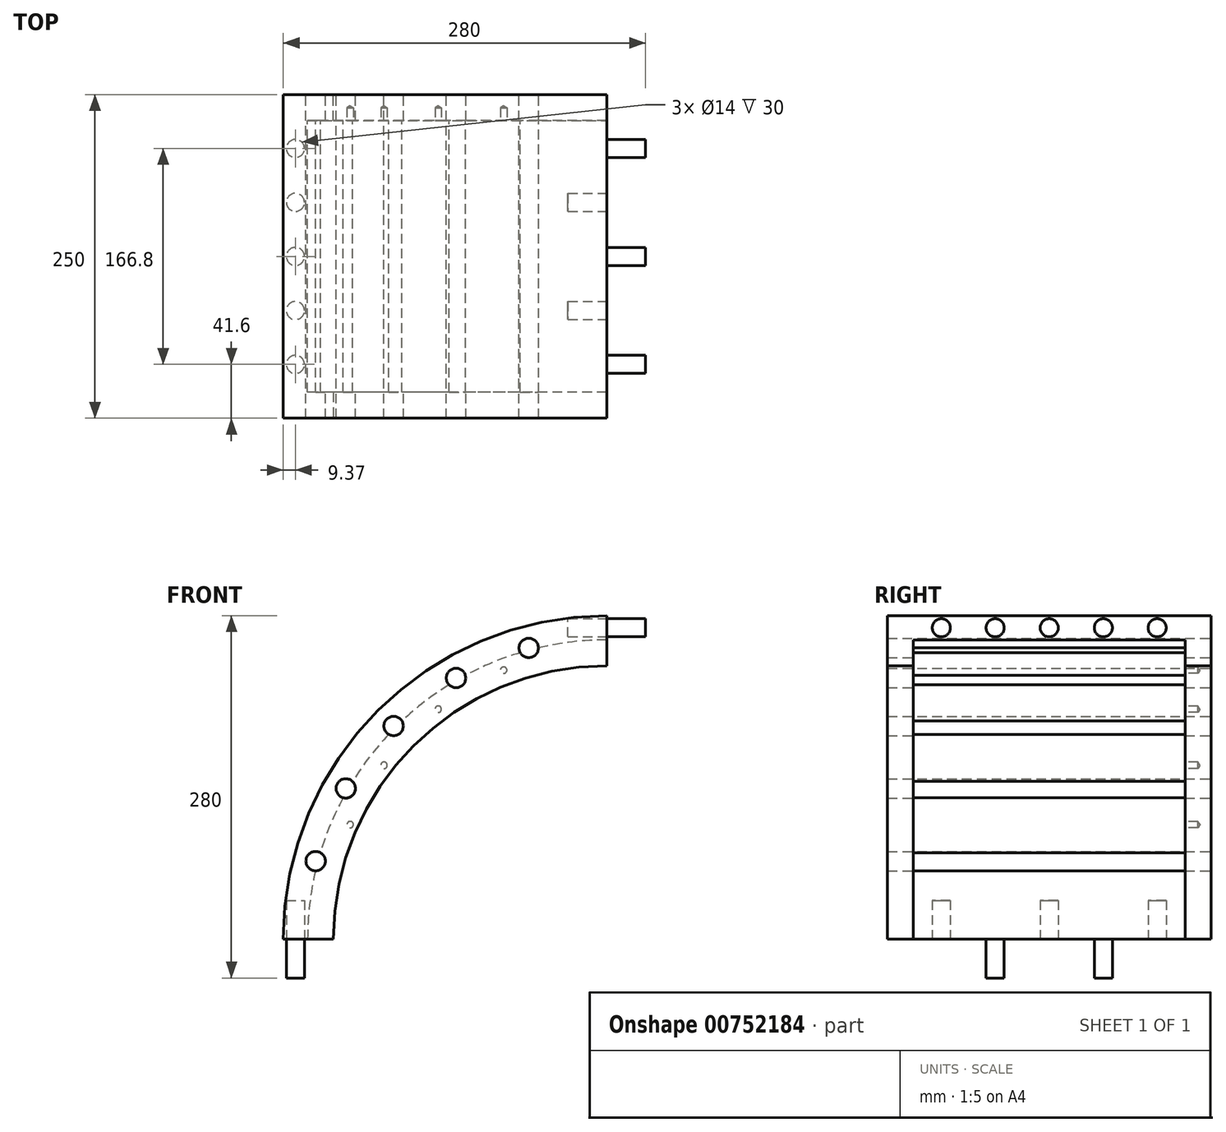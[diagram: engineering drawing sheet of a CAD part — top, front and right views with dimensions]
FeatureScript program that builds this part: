
annotation { "Feature Type Name" : "Feature", "Feature Type Description" : "" }
export const myFeature = defineFeature(function(context is Context, id is Id, definition is map)
    precondition{}
    {
        {
            var Q0;
            Q0=qCreatedBy(makeId("Front.planeOp"),FACE);
            var sketch = newSketch(context, id + "F0", { "sketchPlane" : qUnion([Q0])});
            skLineSegment(sketch, "E0.bottom", {"start": v(-250, 250) * mm, "end": v(250, 250) * mm});
            skLineSegment(sketch, "E0.top", {"start": v(-250, -250) * mm, "end": v(250, -250) * mm});
            skLineSegment(sketch, "E0.left", {"start": v(-250, 250) * mm, "end": v(-250, -250) * mm});
            skLineSegment(sketch, "E0.right", {"start": v(250, 250) * mm, "end": v(250, -250) * mm});
            skPoint(sketch, "E0.middle", {"position": v(0, 0) * mm});
            skCircle(sketch, "E1", {"center": v(0, 0) * mm, "radius": 250 * mm});
            skLineSegment(sketch, "E2", {"start": v(0, 0) * mm, "end": v(0, 250) * mm, "construction": true});
            skLineSegment(sketch, "E3", {"start": v(0, -250) * mm, "end": v(0, 0) * mm, "construction": true});
            skLineSegment(sketch, "E4", {"start": v(-250, 0) * mm, "end": v(250, 0) * mm, "construction": true});
            skCircle(sketch, "E5", {"center": v(0, 0) * mm, "radius": 231.25 * mm});
            skLineSegment(sketch, "E6", {"start": v(0, 250) * mm, "end": v(0, 0) * mm});
            skLineSegment(sketch, "E7", {"start": v(-250, 0) * mm, "end": v(0, 0) * mm});
            skSolve(sketch);
        }
        {
            var Q0;
            {var subQ0=sQuery(id+"F0.wireOp",EDGE,"E6");var subQ5=sQuery(id+"F0.wireOp",EDGE,"E5");var subQ6=makeQuery(id+"F0.imprint","INTERSECT",VERTEX,{"derivedFrom":[subQ5,subQ0]});Q0=makeQuery(id+"F0.imprint","IMPRINT",FACE,{"disambiguationData":[TD([[makeQuery(id+"F0.imprint","IMPRINT",EDGE,{"disambiguationData":[TD([[subQ6,-1.0]])],"derivedFrom":subQ5}),-1.0]])]});}
            extrude(context, id + "F1", {"entities" : qUnion([Q0]), "depth" : 250 * mm, "offsetDistance" : 25 * mm});
        }
        {
            var Q0;
            Q0=makeQuery(id+"F1.opExtrude","SWEPT_FACE",FACE,{"disambiguationData":[OSD([sQuery(id+"F0.wireOp",EDGE,"E6")])]});
            var sketch = newSketch(context, id + "F2", { "sketchPlane" : qUnion([Q0])});
            skLineSegment(sketch, "E8", {"start": v(-250, 240.63) * mm, "end": v(0, 240.63) * mm, "construction": true});
            skLineSegment(sketch, "E9", {"start": v(-125, 250) * mm, "end": v(-125, 231.25) * mm, "construction": true});
            skLineSegment(sketch, "E10", {"start": v(-208.4, 250) * mm, "end": v(-208.4, 231.25) * mm, "construction": true});
            skLineSegment(sketch, "E11", {"start": v(-166.8, 250) * mm, "end": v(-166.8, 231.25) * mm, "construction": true});
            skLineSegment(sketch, "E12", {"start": v(-83.2, 250) * mm, "end": v(-83.2, 231.25) * mm, "construction": true});
            skLineSegment(sketch, "E13", {"start": v(-41.6, 250) * mm, "end": v(-41.6, 231.25) * mm, "construction": true});
            skPoint(sketch, "E14", {"position": v(-208.4, 240.62) * mm});
            skPoint(sketch, "E15", {"position": v(-166.8, 240.62) * mm});
            skPoint(sketch, "E16", {"position": v(-125, 240.63) * mm});
            skPoint(sketch, "E17", {"position": v(-83.2, 240.63) * mm});
            skPoint(sketch, "E18", {"position": v(-41.6, 240.62) * mm});
            skCircle(sketch, "E19", {"center": v(-208.4, 240.62) * mm, "radius": 7 * mm});
            skCircle(sketch, "E20", {"center": v(-166.8, 240.62) * mm, "radius": 7 * mm});
            skCircle(sketch, "E21", {"center": v(-125, 240.63) * mm, "radius": 7 * mm});
            skCircle(sketch, "E22", {"center": v(-83.2, 240.63) * mm, "radius": 7 * mm});
            skCircle(sketch, "E23", {"center": v(-41.6, 240.62) * mm, "radius": 7 * mm});
            skSolve(sketch);
        }
        {
            var Q0;
            Q0=makeQuery(id+"F2.imprint","IMPRINT",FACE,{"disambiguationData":[TD([[makeQuery(id+"F2.imprint","IMPRINT",EDGE,{"derivedFrom":sQuery(id+"F2.wireOp",EDGE,"E19")}),1.0]])]});
            var Q1;
            Q1=makeQuery(id+"F2.imprint","IMPRINT",FACE,{"disambiguationData":[TD([[makeQuery(id+"F2.imprint","IMPRINT",EDGE,{"derivedFrom":sQuery(id+"F2.wireOp",EDGE,"E21")}),1.0]])]});
            var Q2;
            Q2=makeQuery(id+"F2.imprint","IMPRINT",FACE,{"disambiguationData":[TD([[makeQuery(id+"F2.imprint","IMPRINT",EDGE,{"derivedFrom":sQuery(id+"F2.wireOp",EDGE,"E23")}),1.0]])]});
            extrude(context, id + "F3", {"entities" : qUnion([Q0, Q1, Q2]), "operationType" : NewBodyOperationType.ADD, "depth" : 30 * mm, "offsetDistance" : 25 * mm});
        }
        {
            var Q0;
            Q0=makeQuery(id+"F2.imprint","IMPRINT",FACE,{"disambiguationData":[TD([[makeQuery(id+"F2.imprint","IMPRINT",EDGE,{"derivedFrom":sQuery(id+"F2.wireOp",EDGE,"E20")}),1.0]])]});
            var Q1;
            Q1=makeQuery(id+"F2.imprint","IMPRINT",FACE,{"disambiguationData":[TD([[makeQuery(id+"F2.imprint","IMPRINT",EDGE,{"derivedFrom":sQuery(id+"F2.wireOp",EDGE,"E22")}),1.0]])]});
            extrude(context, id + "F4", {"entities" : qUnion([Q0, Q1]), "operationType" : NewBodyOperationType.REMOVE, "oppositeDirection" : true, "depth" : 30 * mm, "offsetDistance" : 25 * mm});
        }
        {
            var Q0;
            Q0=makeQuery(id+"F1.opExtrude","CAP_FACE",FACE,{"disambiguationData":[OSD([sQuery(id+"F0.wireOp",EDGE,"E1"),sQuery(id+"F0.wireOp",EDGE,"E5"),sQuery(id+"F0.wireOp",EDGE,"E6"),sQuery(id+"F0.wireOp",EDGE,"E7")])],"isStart":false});
            var sketch = newSketch(context, id + "F5", { "sketchPlane" : qUnion([Q0])});
            skCircle(sketch, "E24", {"center": v(0, 0) * mm, "radius": 211.25 * mm});
            skPoint(sketch, "E25", {"position": v(-211.25, 0) * mm});
            skPoint(sketch, "E26", {"position": v(0, 211.25) * mm});
            skLineSegment(sketch, "E27", {"start": v(0, 231.25) * mm, "end": v(0, 211.25) * mm});
            skLineSegment(sketch, "E28", {"start": v(-211.25, 0) * mm, "end": v(-231.25, 0) * mm});
            skArc(sketch, "E29", {"start": v(-231.25, 0) * mm, "mid": v(-163.52, 163.52) * mm, "end": v(0, 231.25) * mm});
            skSolve(sketch);
        }
        {
            var Q0;
            {var subQ0=sQuery(id+"F5.wireOp",EDGE,"E27");Q0=makeQuery(id+"F5.imprint","IMPRINT",FACE,{"disambiguationData":[TD([[makeQuery(id+"F5.imprint","IMPRINT",EDGE,{"derivedFrom":subQ0}),-1.0]])]});}
            extrude(context, id + "F6", {"entities" : qUnion([Q0]), "operationType" : NewBodyOperationType.ADD, "oppositeDirection" : true, "depth" : 20 * mm, "offsetDistance" : 25 * mm});
        }
        {
            var Q0;
            Q0=makeQuery(id+"F1.opExtrude","CAP_FACE",FACE,{"disambiguationData":[OSD([sQuery(id+"F0.wireOp",EDGE,"E1"),sQuery(id+"F0.wireOp",EDGE,"E5"),sQuery(id+"F0.wireOp",EDGE,"E6"),sQuery(id+"F0.wireOp",EDGE,"E7")])],"isStart":true});
            var sketch = newSketch(context, id + "F7", { "sketchPlane" : qUnion([Q0])});
            skCircle(sketch, "E30", {"center": v(0, 0) * mm, "radius": 211.25 * mm});
            skLineSegment(sketch, "E31", {"start": v(0, 231.25) * mm, "end": v(0, 211.25) * mm});
            skLineSegment(sketch, "E32", {"start": v(231.25, 0) * mm, "end": v(211.25, 0) * mm});
            skSolve(sketch);
        }
        {
            var Q0;
            {var subQ0=sQuery(id+"F7.wireOp",EDGE,"E31");Q0=makeQuery(id+"F7.imprint","IMPRINT",FACE,{"disambiguationData":[TD([[makeQuery(id+"F7.imprint","IMPRINT",EDGE,{"derivedFrom":subQ0}),1.0]])]});}
            extrude(context, id + "F8", {"entities" : qUnion([Q0]), "operationType" : NewBodyOperationType.ADD, "oppositeDirection" : true, "depth" : 20 * mm, "offsetDistance" : 25 * mm});
        }
        {
            var Q0;
            Q0=makeQuery(id+"F8.boolean.opBoolean","MERGE",FACE,{"derivedFrom":[makeQuery(id+"F6.boolean.opBoolean","MERGE",FACE,{"derivedFrom":[makeQuery(id+"F1.opExtrude","SWEPT_FACE",FACE,{"disambiguationData":[OSD([sQuery(id+"F0.wireOp",EDGE,"E7")])]}),makeQuery(id+"F6.opExtrude","SWEPT_FACE",FACE,{"disambiguationData":[OSD([sQuery(id+"F5.wireOp",EDGE,"E28")])]})]}),makeQuery(id+"F8.opExtrude","SWEPT_FACE",FACE,{"disambiguationData":[OSD([sQuery(id+"F7.wireOp",EDGE,"E32")])]})]});
            var sketch = newSketch(context, id + "F9", { "sketchPlane" : qUnion([Q0])});
            skLineSegment(sketch, "E33", {"start": v(-231.25, 125) * mm, "end": v(-250, 125) * mm, "construction": true});
            skLineSegment(sketch, "E34", {"start": v(-250, 41.6) * mm, "end": v(-231.25, 41.6) * mm});
            skLineSegment(sketch, "E35", {"start": v(-250, 83.2) * mm, "end": v(-231.25, 83.2) * mm});
            skLineSegment(sketch, "E36", {"start": v(-250, 208.4) * mm, "end": v(-231.25, 208.4) * mm});
            skLineSegment(sketch, "E37", {"start": v(-250, 166.8) * mm, "end": v(-231.25, 166.8) * mm});
            skLineSegment(sketch, "E38", {"start": v(-250, 125) * mm, "end": v(-231.25, 125) * mm});
            skLineSegment(sketch, "E39", {"start": v(-240.63, 41.6) * mm, "end": v(-240.63, 250) * mm});
            skLineSegment(sketch, "E40", {"start": v(-240.63, 250) * mm, "end": v(-240.63, 0) * mm});
            skCircle(sketch, "E41", {"center": v(-240.63, 208.4) * mm, "radius": 7 * mm});
            skCircle(sketch, "E42", {"center": v(-240.63, 166.8) * mm, "radius": 7 * mm});
            skCircle(sketch, "E43", {"center": v(-240.63, 125) * mm, "radius": 7 * mm});
            skCircle(sketch, "E44", {"center": v(-240.63, 83.2) * mm, "radius": 7 * mm});
            skCircle(sketch, "E45", {"center": v(-240.63, 41.6) * mm, "radius": 7 * mm});
            skSolve(sketch);
        }
        {
            var Q0;
            {var subQ0=sQuery(id+"F9.wireOp",EDGE,"E40");var subQ1=sQuery(id+"F9.wireOp",EDGE,"E37");var subQ2=makeQuery(id+"F9.imprint","INTERSECT",VERTEX,{"derivedFrom":[subQ1,subQ0]});Q0=makeQuery(id+"F9.imprint","IMPRINT",FACE,{"disambiguationData":[TD([[makeQuery(id+"F9.imprint","IMPRINT",EDGE,{"disambiguationData":[TD([[subQ2,-1.0]])],"derivedFrom":subQ1}),1.0]])]});}
            var Q1;
            {var subQ0=sQuery(id+"F9.wireOp",EDGE,"E40");var subQ1=sQuery(id+"F9.wireOp",EDGE,"E37");var subQ2=makeQuery(id+"F9.imprint","INTERSECT",VERTEX,{"derivedFrom":[subQ1,subQ0]});Q1=makeQuery(id+"F9.imprint","IMPRINT",FACE,{"disambiguationData":[TD([[makeQuery(id+"F9.imprint","IMPRINT",EDGE,{"disambiguationData":[TD([[subQ2,-1.0]])],"derivedFrom":subQ1}),-1.0]])]});}
            var Q2;
            {var subQ0=sQuery(id+"F9.wireOp",EDGE,"E42");var subQ1=sQuery(id+"F9.wireOp",EDGE,"E37");var subQ2=makeQuery(id+"F9.imprint","INTERSECT",VERTEX,{"disambiguationData":[OD(0.0)],"derivedFrom":[subQ1,subQ0]});Q2=makeQuery(id+"F9.imprint","IMPRINT",FACE,{"disambiguationData":[TD([[makeQuery(id+"F9.imprint","IMPRINT",EDGE,{"disambiguationData":[TD([[subQ2,-1.0]])],"derivedFrom":subQ1}),-1.0]])]});}
            var Q3;
            {var subQ0=sQuery(id+"F9.wireOp",EDGE,"E42");var subQ1=sQuery(id+"F9.wireOp",EDGE,"E37");var subQ2=makeQuery(id+"F9.imprint","INTERSECT",VERTEX,{"disambiguationData":[OD(0.0)],"derivedFrom":[subQ1,subQ0]});Q3=makeQuery(id+"F9.imprint","IMPRINT",FACE,{"disambiguationData":[TD([[makeQuery(id+"F9.imprint","IMPRINT",EDGE,{"disambiguationData":[TD([[subQ2,-1.0]])],"derivedFrom":subQ1}),1.0]])]});}
            var Q4;
            {var subQ0=sQuery(id+"F9.wireOp",EDGE,"E40");var subQ1=sQuery(id+"F9.wireOp",EDGE,"E35");var subQ2=makeQuery(id+"F9.imprint","INTERSECT",VERTEX,{"derivedFrom":[subQ1,subQ0]});Q4=makeQuery(id+"F9.imprint","IMPRINT",FACE,{"disambiguationData":[TD([[makeQuery(id+"F9.imprint","IMPRINT",EDGE,{"disambiguationData":[TD([[subQ2,-1.0]])],"derivedFrom":subQ1}),1.0]])]});}
            var Q5;
            {var subQ0=sQuery(id+"F9.wireOp",EDGE,"E40");var subQ1=sQuery(id+"F9.wireOp",EDGE,"E35");var subQ2=makeQuery(id+"F9.imprint","INTERSECT",VERTEX,{"derivedFrom":[subQ1,subQ0]});Q5=makeQuery(id+"F9.imprint","IMPRINT",FACE,{"disambiguationData":[TD([[makeQuery(id+"F9.imprint","IMPRINT",EDGE,{"disambiguationData":[TD([[subQ2,-1.0]])],"derivedFrom":subQ1}),-1.0]])]});}
            var Q6;
            {var subQ0=sQuery(id+"F9.wireOp",EDGE,"E44");var subQ1=sQuery(id+"F9.wireOp",EDGE,"E35");var subQ2=makeQuery(id+"F9.imprint","INTERSECT",VERTEX,{"disambiguationData":[OD(0.0)],"derivedFrom":[subQ1,subQ0]});Q6=makeQuery(id+"F9.imprint","IMPRINT",FACE,{"disambiguationData":[TD([[makeQuery(id+"F9.imprint","IMPRINT",EDGE,{"disambiguationData":[TD([[subQ2,-1.0]])],"derivedFrom":subQ1}),1.0]])]});}
            var Q7;
            {var subQ0=sQuery(id+"F9.wireOp",EDGE,"E44");var subQ1=sQuery(id+"F9.wireOp",EDGE,"E35");var subQ2=makeQuery(id+"F9.imprint","INTERSECT",VERTEX,{"disambiguationData":[OD(0.0)],"derivedFrom":[subQ1,subQ0]});Q7=makeQuery(id+"F9.imprint","IMPRINT",FACE,{"disambiguationData":[TD([[makeQuery(id+"F9.imprint","IMPRINT",EDGE,{"disambiguationData":[TD([[subQ2,-1.0]])],"derivedFrom":subQ1}),-1.0]])]});}
            extrude(context, id + "F10", {"entities" : qUnion([Q0, Q1, Q2, Q3, Q4, Q5, Q6, Q7]), "operationType" : NewBodyOperationType.ADD, "depth" : 30 * mm, "offsetDistance" : 25 * mm});
        }
        {
            var Q0;
            {var subQ0=sQuery(id+"F9.wireOp",EDGE,"E41");var subQ1=sQuery(id+"F9.wireOp",EDGE,"E36");var subQ2=makeQuery(id+"F9.imprint","INTERSECT",VERTEX,{"disambiguationData":[OD(0.0)],"derivedFrom":[subQ1,subQ0]});Q0=makeQuery(id+"F9.imprint","IMPRINT",FACE,{"disambiguationData":[TD([[makeQuery(id+"F9.imprint","IMPRINT",EDGE,{"disambiguationData":[TD([[subQ2,-1.0]])],"derivedFrom":subQ1}),1.0]])]});}
            var Q1;
            {var subQ0=sQuery(id+"F9.wireOp",EDGE,"E40");var subQ1=sQuery(id+"F9.wireOp",EDGE,"E36");var subQ2=makeQuery(id+"F9.imprint","INTERSECT",VERTEX,{"derivedFrom":[subQ1,subQ0]});Q1=makeQuery(id+"F9.imprint","IMPRINT",FACE,{"disambiguationData":[TD([[makeQuery(id+"F9.imprint","IMPRINT",EDGE,{"disambiguationData":[TD([[subQ2,-1.0]])],"derivedFrom":subQ1}),1.0]])]});}
            var Q2;
            {var subQ0=sQuery(id+"F9.wireOp",EDGE,"E40");var subQ1=sQuery(id+"F9.wireOp",EDGE,"E36");var subQ2=makeQuery(id+"F9.imprint","INTERSECT",VERTEX,{"derivedFrom":[subQ1,subQ0]});Q2=makeQuery(id+"F9.imprint","IMPRINT",FACE,{"disambiguationData":[TD([[makeQuery(id+"F9.imprint","IMPRINT",EDGE,{"disambiguationData":[TD([[subQ2,-1.0]])],"derivedFrom":subQ1}),-1.0]])]});}
            var Q3;
            {var subQ0=sQuery(id+"F9.wireOp",EDGE,"E40");var subQ1=sQuery(id+"F9.wireOp",EDGE,"E38");var subQ2=makeQuery(id+"F9.imprint","INTERSECT",VERTEX,{"derivedFrom":[subQ1,subQ0]});Q3=makeQuery(id+"F9.imprint","IMPRINT",FACE,{"disambiguationData":[TD([[makeQuery(id+"F9.imprint","IMPRINT",EDGE,{"disambiguationData":[TD([[subQ2,-1.0]])],"derivedFrom":subQ1}),1.0]])]});}
            var Q4;
            {var subQ0=sQuery(id+"F9.wireOp",EDGE,"E43");var subQ1=sQuery(id+"F9.wireOp",EDGE,"E38");var subQ2=makeQuery(id+"F9.imprint","INTERSECT",VERTEX,{"disambiguationData":[OD(0.0)],"derivedFrom":[subQ1,subQ0]});Q4=makeQuery(id+"F9.imprint","IMPRINT",FACE,{"disambiguationData":[TD([[makeQuery(id+"F9.imprint","IMPRINT",EDGE,{"disambiguationData":[TD([[subQ2,-1.0]])],"derivedFrom":subQ1}),-1.0]])]});}
            var Q5;
            {var subQ0=sQuery(id+"F9.wireOp",EDGE,"E40");var subQ1=sQuery(id+"F9.wireOp",EDGE,"E38");var subQ2=makeQuery(id+"F9.imprint","INTERSECT",VERTEX,{"derivedFrom":[subQ1,subQ0]});Q5=makeQuery(id+"F9.imprint","IMPRINT",FACE,{"disambiguationData":[TD([[makeQuery(id+"F9.imprint","IMPRINT",EDGE,{"disambiguationData":[TD([[subQ2,-1.0]])],"derivedFrom":subQ1}),-1.0]])]});}
            var Q6;
            {var subQ0=sQuery(id+"F9.wireOp",EDGE,"E43");var subQ1=sQuery(id+"F9.wireOp",EDGE,"E38");var subQ2=makeQuery(id+"F9.imprint","INTERSECT",VERTEX,{"disambiguationData":[OD(0.0)],"derivedFrom":[subQ1,subQ0]});Q6=makeQuery(id+"F9.imprint","IMPRINT",FACE,{"disambiguationData":[TD([[makeQuery(id+"F9.imprint","IMPRINT",EDGE,{"disambiguationData":[TD([[subQ2,-1.0]])],"derivedFrom":subQ1}),1.0]])]});}
            var Q7;
            {var subQ0=sQuery(id+"F9.wireOp",EDGE,"E40");var subQ1=sQuery(id+"F9.wireOp",EDGE,"E34");var subQ2=makeQuery(id+"F9.imprint","INTERSECT",VERTEX,{"derivedFrom":[subQ1,subQ0]});Q7=makeQuery(id+"F9.imprint","IMPRINT",FACE,{"disambiguationData":[TD([[makeQuery(id+"F9.imprint","IMPRINT",EDGE,{"disambiguationData":[TD([[subQ2,-1.0]])],"derivedFrom":subQ1}),1.0]])]});}
            var Q8;
            {var subQ0=sQuery(id+"F9.wireOp",EDGE,"E40");var subQ1=sQuery(id+"F9.wireOp",EDGE,"E34");var subQ2=makeQuery(id+"F9.imprint","INTERSECT",VERTEX,{"derivedFrom":[subQ1,subQ0]});Q8=makeQuery(id+"F9.imprint","IMPRINT",FACE,{"disambiguationData":[TD([[makeQuery(id+"F9.imprint","IMPRINT",EDGE,{"disambiguationData":[TD([[subQ2,-1.0]])],"derivedFrom":subQ1}),-1.0]])]});}
            var Q9;
            {var subQ0=sQuery(id+"F9.wireOp",EDGE,"E45");var subQ1=sQuery(id+"F9.wireOp",EDGE,"E34");var subQ2=makeQuery(id+"F9.imprint","INTERSECT",VERTEX,{"disambiguationData":[OD(0.0)],"derivedFrom":[subQ1,subQ0]});Q9=makeQuery(id+"F9.imprint","IMPRINT",FACE,{"disambiguationData":[TD([[makeQuery(id+"F9.imprint","IMPRINT",EDGE,{"disambiguationData":[TD([[subQ2,-1.0]])],"derivedFrom":subQ1}),1.0]])]});}
            var Q10;
            {var subQ0=sQuery(id+"F9.wireOp",EDGE,"E45");var subQ1=sQuery(id+"F9.wireOp",EDGE,"E34");var subQ2=makeQuery(id+"F9.imprint","INTERSECT",VERTEX,{"disambiguationData":[OD(0.0)],"derivedFrom":[subQ1,subQ0]});Q10=makeQuery(id+"F9.imprint","IMPRINT",FACE,{"disambiguationData":[TD([[makeQuery(id+"F9.imprint","IMPRINT",EDGE,{"disambiguationData":[TD([[subQ2,-1.0]])],"derivedFrom":subQ1}),-1.0]])]});}
            var Q11;
            {var subQ0=sQuery(id+"F9.wireOp",EDGE,"E41");var subQ1=sQuery(id+"F9.wireOp",EDGE,"E36");var subQ2=makeQuery(id+"F9.imprint","INTERSECT",VERTEX,{"disambiguationData":[OD(0.0)],"derivedFrom":[subQ1,subQ0]});Q11=makeQuery(id+"F9.imprint","IMPRINT",FACE,{"disambiguationData":[TD([[makeQuery(id+"F9.imprint","IMPRINT",EDGE,{"disambiguationData":[TD([[subQ2,-1.0]])],"derivedFrom":subQ1}),-1.0]])]});}
            extrude(context, id + "F11", {"entities" : qUnion([Q0, Q1, Q2, Q3, Q4, Q5, Q6, Q7, Q8, Q9, Q10, Q11]), "operationType" : NewBodyOperationType.REMOVE, "oppositeDirection" : true, "depth" : 30 * mm, "offsetDistance" : 25 * mm});
        }
        {
            var Q0;
            {var subQ0=sQuery(id+"F0.wireOp",EDGE,"E5");Q0=makeQuery(id+"F8.boolean.opBoolean","MERGE",FACE,{"derivedFrom":[makeQuery(id+"F1.opExtrude","CAP_FACE",FACE,{"disambiguationData":[OSD([sQuery(id+"F0.wireOp",EDGE,"E1"),subQ0,sQuery(id+"F0.wireOp",EDGE,"E6"),sQuery(id+"F0.wireOp",EDGE,"E7")])],"isStart":true}),makeQuery(id+"F8.opExtrude","CAP_FACE",FACE,{"disambiguationData":[OSD([subQ0,sQuery(id+"F7.wireOp",EDGE,"E30"),sQuery(id+"F7.wireOp",EDGE,"E31"),sQuery(id+"F7.wireOp",EDGE,"E32")])],"isStart":true})]});}
            var sketch = newSketch(context, id + "F12", { "sketchPlane" : qUnion([Q0])});
            skLineSegment(sketch, "E46", {"start": v(0, 0) * mm, "end": v(0, 232.97) * mm, "construction": true});
            skLineSegment(sketch, "E47", {"start": v(0, 0) * mm, "end": v(232.97, 0) * mm, "construction": true});
            skLineSegment(sketch, "E48", {"start": v(0, 0) * mm, "end": v(164.73, 164.73) * mm, "construction": true});
            skLineSegment(sketch, "E49", {"start": v(0, 0) * mm, "end": v(116.48, 201.76) * mm, "construction": true});
            skLineSegment(sketch, "E50", {"start": v(0, 0) * mm, "end": v(201.76, 116.48) * mm, "construction": true});
            skLineSegment(sketch, "E51", {"start": v(0, 0) * mm, "end": v(60.3, 225.03) * mm, "construction": true});
            skLineSegment(sketch, "E52", {"start": v(0, 0) * mm, "end": v(225.03, 60.3) * mm, "construction": true});
            skLineSegment(sketch, "E53", {"start": v(0, 232.97) * mm, "end": v(60.3, 225.03) * mm, "construction": true});
            skLineSegment(sketch, "E54", {"start": v(60.3, 225.03) * mm, "end": v(116.48, 201.76) * mm, "construction": true});
            skLineSegment(sketch, "E55", {"start": v(116.48, 201.76) * mm, "end": v(164.73, 164.73) * mm, "construction": true});
            skLineSegment(sketch, "E56", {"start": v(164.73, 164.73) * mm, "end": v(201.76, 116.48) * mm, "construction": true});
            skLineSegment(sketch, "E57", {"start": v(201.76, 116.48) * mm, "end": v(225.03, 60.3) * mm, "construction": true});
            skLineSegment(sketch, "E58", {"start": v(225.03, 60.3) * mm, "end": v(232.97, 0) * mm, "construction": true});
            skPoint(sketch, "E59", {"position": v(60.3, 225.03) * mm});
            skPoint(sketch, "E60", {"position": v(116.48, 201.76) * mm});
            skPoint(sketch, "E61", {"position": v(164.73, 164.73) * mm});
            skPoint(sketch, "E62", {"position": v(201.76, 116.48) * mm});
            skPoint(sketch, "E63", {"position": v(225.03, 60.3) * mm});
            skLineSegment(sketch, "E64", {"start": v(247.82, 32.98) * mm, "end": v(0, 0) * mm, "construction": true});
            skSolve(sketch);
        }
        {
            var Q0;
            Q0=sQuery(id+"F12.wireOp",VERTEX,"E59");
            var Q1;
            Q1=sQuery(id+"F12.wireOp",VERTEX,"E60");
            var Q2;
            Q2=sQuery(id+"F12.wireOp",VERTEX,"E61");
            var Q3;
            Q3=sQuery(id+"F12.wireOp",VERTEX,"E62");
            var Q4;
            Q4=sQuery(id+"F12.wireOp",VERTEX,"E63");
            var Q5;
            Q5=makeQuery(id+"F1.opExtrude","SWEPT_BODY",BODY,{"disambiguationData":[OSD([sQuery(id+"F0.wireOp",EDGE,"E1"),sQuery(id+"F0.wireOp",EDGE,"E5"),sQuery(id+"F0.wireOp",EDGE,"E6"),sQuery(id+"F0.wireOp",EDGE,"E7")])]});
            hole(context, id + "F13", {"style" : HoleStyle.SIMPLE, "endStyle" : HoleEndStyle.BLIND, "holeDiameter" : 15 * mm, "majorDiameter" : 5 * mm, "holeDepth" : 400 * mm, "isTappedThrough" : true, "tappedDepth" : 12 * mm, "tapClearance" : 3, "startFromSketch" : true, "locations" : qUnion([Q0, Q1, Q2, Q3, Q4]), "scope" : qUnion([Q5])});
        }
        {
            var Q0;
            Q0=makeQuery(id+"F8.opExtrude","CAP_FACE",FACE,{"disambiguationData":[OSD([sQuery(id+"F0.wireOp",EDGE,"E5"),sQuery(id+"F7.wireOp",EDGE,"E30"),sQuery(id+"F7.wireOp",EDGE,"E31"),sQuery(id+"F7.wireOp",EDGE,"E32")])],"isStart":false});
            var sketch = newSketch(context, id + "F14", { "sketchPlane" : qUnion([Q0])});
            skCircle(sketch, "E65", {"center": v(10.03, 0) * mm, "radius": 226.37 * mm});
            skPoint(sketch, "E66", {"position": v(-79.68, 207.84) * mm});
            skPoint(sketch, "E67", {"position": v(-130.25, 177.67) * mm});
            skPoint(sketch, "E68", {"position": v(-172.18, 134.33) * mm});
            skPoint(sketch, "E69", {"position": v(-198.33, 88.5) * mm});
            skPoint(sketch, "E69.positionSnap0", {"position": v(-213.65, 88.5) * mm});
            skSolve(sketch);
        }
        {
            var Q0;
            Q0=sQuery(id+"F14.wireOp",VERTEX,"E69");
            var Q1;
            Q1=sQuery(id+"F14.wireOp",VERTEX,"E68");
            var Q2;
            Q2=sQuery(id+"F14.wireOp",VERTEX,"E67");
            var Q3;
            Q3=sQuery(id+"F14.wireOp",VERTEX,"E66");
            var Q4;
            Q4=makeQuery(id+"F1.opExtrude","SWEPT_BODY",BODY,{"disambiguationData":[OSD([sQuery(id+"F0.wireOp",EDGE,"E1"),sQuery(id+"F0.wireOp",EDGE,"E5"),sQuery(id+"F0.wireOp",EDGE,"E6"),sQuery(id+"F0.wireOp",EDGE,"E7")])]});
            hole(context, id + "F15", {"style" : HoleStyle.SIMPLE, "endStyle" : HoleEndStyle.BLIND, "holeDiameter" : 5 * mm, "majorDiameter" : 5 * mm, "holeDepth" : 10 * mm, "isTappedThrough" : true, "tappedDepth" : 12 * mm, "tapClearance" : 3, "startFromSketch" : true, "locations" : qUnion([Q0, Q1, Q2, Q3]), "scope" : qUnion([Q4])});
        }
    });
